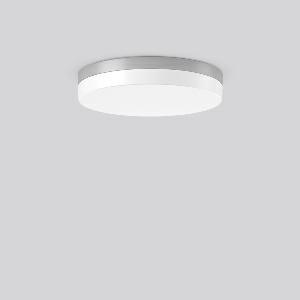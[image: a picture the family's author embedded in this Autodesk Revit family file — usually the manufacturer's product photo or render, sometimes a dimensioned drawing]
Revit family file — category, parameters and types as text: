
# Revit family: flat_slim_round_312631_004_19_48ac
name_source: partatom
category: Lighting Fixtures
units: mm (PartAtom-declared; Revit-internal decimal feet)

## family parameters
Cut with Voids When Loaded = No
Host = Face
Light Source = No
Part Type = Normal
Room Calculation Point = No
Round Connector Dimension = Use Diameter
Shared = No

## types (1)
- MultiLumen 1 830 (1 x LED Modul 830, 2450 lm, 3000)
    Apparent Load = 25 VA
    CIE Flux Codes = 40 70 90 84 100
    Color Rendering = 80
    Color Temperature = 3000
    Default Elevation = 1800 mm
    Height = 75 mm
    Lamp = 1 x LED Modul 830
    Lamp Light Flux = 2450 lm
    Lamp count = 1
    Length = 400 mm
    Lifetime = 50000 h
    Luminous efficacy = 98 lm/W
    Manufacturer = RZB
    ModVariant = No
    Model = 312631.004.19
    Mounting Place = Ceiling
    Mounting Type = Surface mounted
    Number of Poles = 1
    OnlyDefault = Yes
    Power Factor = 1
    Product Name = FLAT SLIM round
    Product group = Surface mounted ceiling and wall luminaires
    ProductGroupID = 305
    Protection Class = Protection class I
    Protection Degree = Degree of protection
    RLX_Detail_Level = 1
    RLX_Emergency_Light_Flux = 0 lm
    RLX_Emergency_Type = 0
    RLX_Emergency_Type_DB = No
    RlxData = <blob elided: 20997 chars, md5=2dab7d7b>
    Socket = socket
    Standby Power = 0 W
    System Light Flux = 2450 lm
    System Power = 25 W
    Type Comments = MultiLumen 1 830
    Type Image = 312631.004.jpg
    URL = http://relux.com
    VarID = multilumen_1_830
    Voltage = 0 V
    Weight = 0.00 kg
    Width = 0 mm  [stored 0 ft]

note: [stored X ft] marks values corroborated as IEEE doubles in the binary element streams (Revit-internal decimal feet)

## geometry (parser evidence)
native form markers: Blend x4, Sweep x13
no freeform markers — native parametric forms only
